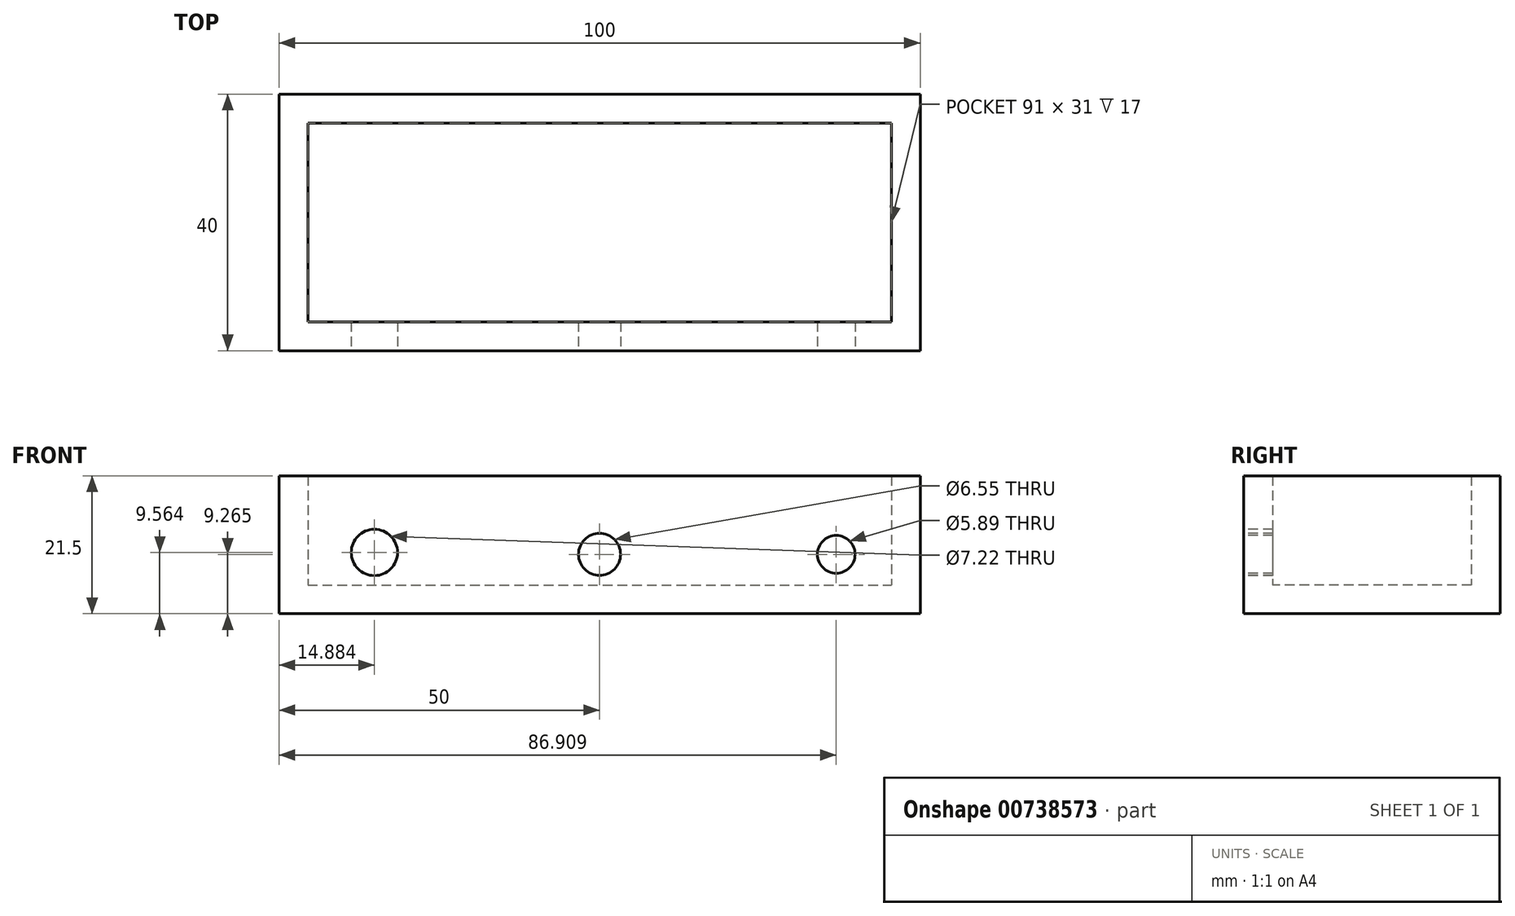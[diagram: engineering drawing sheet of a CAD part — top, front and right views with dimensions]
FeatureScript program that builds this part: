
annotation { "Feature Type Name" : "Feature", "Feature Type Description" : "" }
export const myFeature = defineFeature(function(context is Context, id is Id, definition is map)
    precondition{}
    {
        {
            var Q0;
            Q0=qCreatedBy(makeId("Top.planeOp"),FACE);
            var sketch = newSketch(context, id + "F0", { "sketchPlane" : qUnion([Q0])});
            skLineSegment(sketch, "E0.bottom", {"start": v(-50, 20) * mm, "end": v(50, 20) * mm});
            skLineSegment(sketch, "E0.top", {"start": v(-50, -20) * mm, "end": v(50, -20) * mm});
            skLineSegment(sketch, "E0.left", {"start": v(-50, 20) * mm, "end": v(-50, -20) * mm});
            skLineSegment(sketch, "E0.right", {"start": v(50, 20) * mm, "end": v(50, -20) * mm});
            skPoint(sketch, "E0.middle", {"position": v(0, 0) * mm});
            skSolve(sketch);
        }
        {
            var Q0;
            Q0=makeQuery(id+"F0.imprint","IMPRINT",FACE,{"disambiguationData":[TD([[makeQuery(id+"F0.imprint","IMPRINT",EDGE,{"derivedFrom":sQuery(id+"F0.wireOp",EDGE,"E0.bottom")}),-1.0]])]});
            extrude(context, id + "F1", {"entities" : qUnion([Q0]), "depth" : 4.5 * mm, "offsetDistance" : 25 * mm});
        }
        {
            var Q0;
            Q0=makeQuery(id+"F1.opExtrude","CAP_FACE",FACE,{"disambiguationData":[OSD([sQuery(id+"F0.wireOp",EDGE,"E0.bottom"),sQuery(id+"F0.wireOp",EDGE,"E0.top"),sQuery(id+"F0.wireOp",EDGE,"E0.left"),sQuery(id+"F0.wireOp",EDGE,"E0.right")])],"isStart":false});
            var sketch = newSketch(context, id + "F2", { "sketchPlane" : qUnion([Q0])});
            skLineSegment(sketch, "E1.bottom", {"start": v(-50, 20) * mm, "end": v(50, 20) * mm});
            skLineSegment(sketch, "E1.top", {"start": v(-50, -20) * mm, "end": v(50, -20) * mm});
            skLineSegment(sketch, "E1.left", {"start": v(-50, 20) * mm, "end": v(-50, -20) * mm});
            skLineSegment(sketch, "E1.right", {"start": v(50, 20) * mm, "end": v(50, -20) * mm});
            skPoint(sketch, "E1.middle", {"position": v(0, 0) * mm});
            skLineSegment(sketch, "E2.0", {"start": v(-45.5, 15.5) * mm, "end": v(45.5, 15.5) * mm});
            skLineSegment(sketch, "E2.1", {"start": v(-45.5, 15.5) * mm, "end": v(-45.5, -15.5) * mm});
            skLineSegment(sketch, "E2.2", {"start": v(-45.5, -15.5) * mm, "end": v(45.5, -15.5) * mm});
            skLineSegment(sketch, "E2.3", {"start": v(45.5, 15.5) * mm, "end": v(45.5, -15.5) * mm});
            skSolve(sketch);
        }
        {
            var Q0;
            Q0 = qSketchRegion(id + "F2", true);
            extrude(context, id + "F3", {"entities" : qUnion([Q0]), "operationType" : NewBodyOperationType.ADD, "depth" : 17 * mm, "offsetDistance" : 25 * mm});
        }
        {
            var Q0;
            Q0=makeQuery(id+"F3.boolean.opBoolean","MERGE",FACE,{"derivedFrom":[makeQuery(id+"F1.opExtrude","SWEPT_FACE",FACE,{"disambiguationData":[OSD([sQuery(id+"F0.wireOp",EDGE,"E0.top")])]}),makeQuery(id+"F3.opExtrude","SWEPT_FACE",FACE,{"disambiguationData":[OSD([sQuery(id+"F2.wireOp",EDGE,"E1.top")])]})]});
            var sketch = newSketch(context, id + "F4", { "sketchPlane" : qUnion([Q0])});
            skPoint(sketch, "E3.center.orphan", {"position": v(0, 9.26) * mm});
            skCircle(sketch, "E4", {"center": v(0, 9.26) * mm, "radius": 3.28 * mm});
            skCircle(sketch, "E5", {"center": v(36.9, 9.26) * mm, "radius": 2.94 * mm});
            skCircle(sketch, "E6", {"center": v(-35.12, 9.56) * mm, "radius": 3.61 * mm});
            skSolve(sketch);
        }
        {
            var Q0;
            Q0 = qSketchRegion(id + "F4", true);
            extrude(context, id + "F5", {"entities" : qUnion([Q0]), "operationType" : NewBodyOperationType.REMOVE, "oppositeDirection" : true, "depth" : 25 * mm, "offsetDistance" : 25 * mm});
        }
    });
